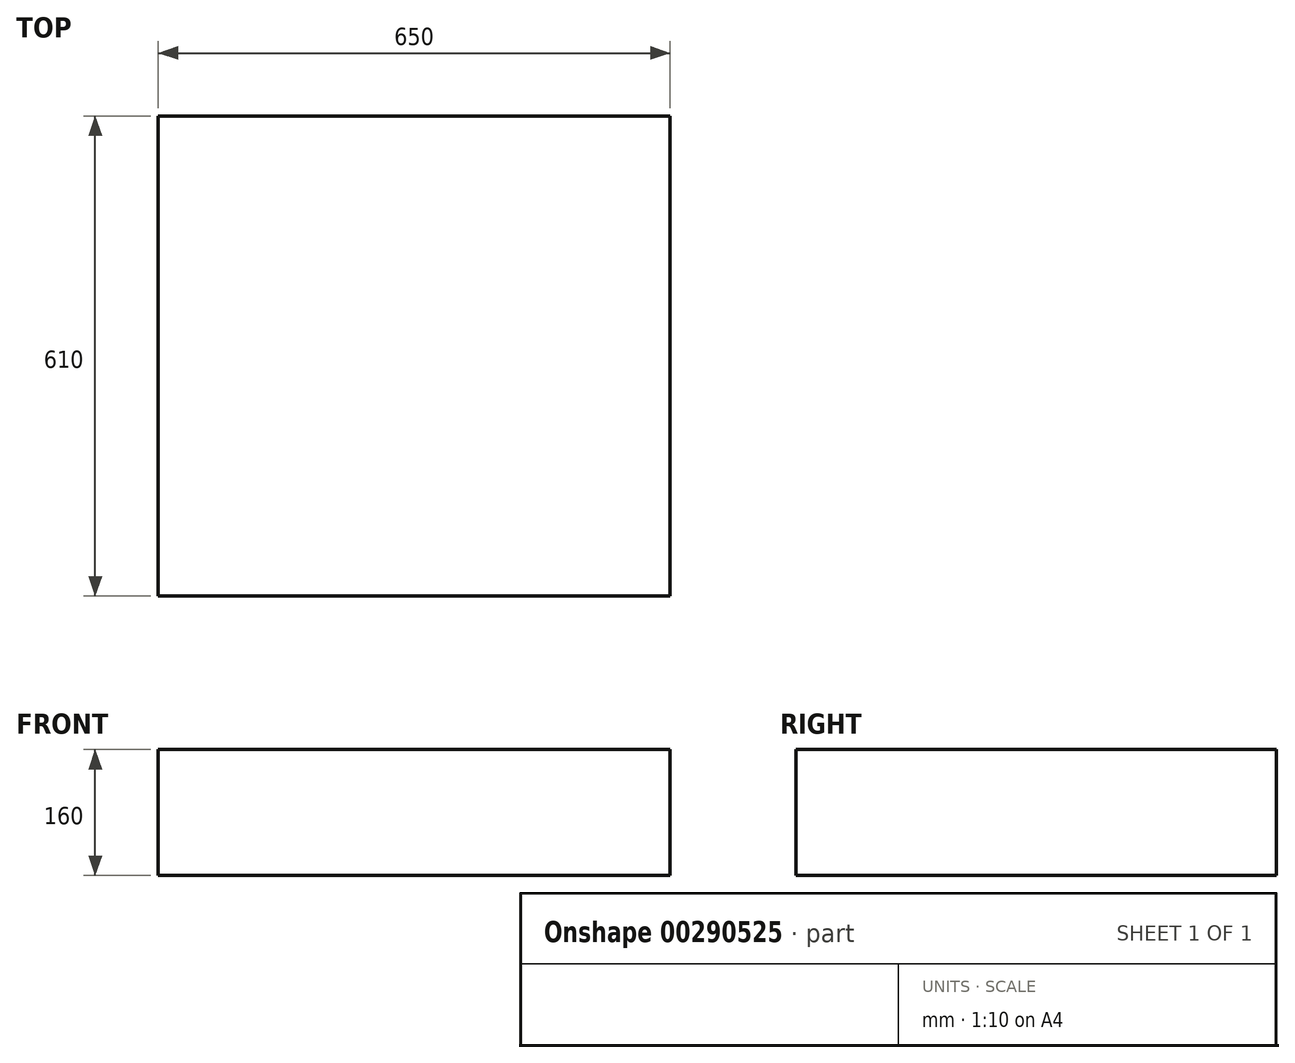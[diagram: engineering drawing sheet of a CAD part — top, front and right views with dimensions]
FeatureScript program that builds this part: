
annotation { "Feature Type Name" : "Feature", "Feature Type Description" : "" }
export const myFeature = defineFeature(function(context is Context, id is Id, definition is map)
    precondition{}
    {
        {
            var Q0;
            Q0=qCreatedBy(makeId("Top.planeOp"),FACE);
            var sketch = newSketch(context, id + "F0", { "sketchPlane" : qUnion([Q0])});
            skLineSegment(sketch, "E0.bottom", {"start": v(325, -305) * mm, "end": v(-325, -305) * mm});
            skLineSegment(sketch, "E0.top", {"start": v(325, 305) * mm, "end": v(-325, 305) * mm});
            skLineSegment(sketch, "E0.left", {"start": v(325, -305) * mm, "end": v(325, 305) * mm});
            skLineSegment(sketch, "E0.right", {"start": v(-325, -305) * mm, "end": v(-325, 305) * mm});
            skPoint(sketch, "E0.middle", {"position": v(0, 0) * mm});
            skSolve(sketch);
        }
        {
            var Q0;
            Q0=makeQuery(id+"F0.imprint","IMPRINT",FACE,{"disambiguationData":[TD([[makeQuery(id+"F0.imprint","IMPRINT",EDGE,{"derivedFrom":sQuery(id+"F0.wireOp",EDGE,"E0.bottom")}),-1.0]])]});
            extrude(context, id + "F1", {"entities" : qUnion([Q0]), "depth" : 160 * mm});
        }
    });
